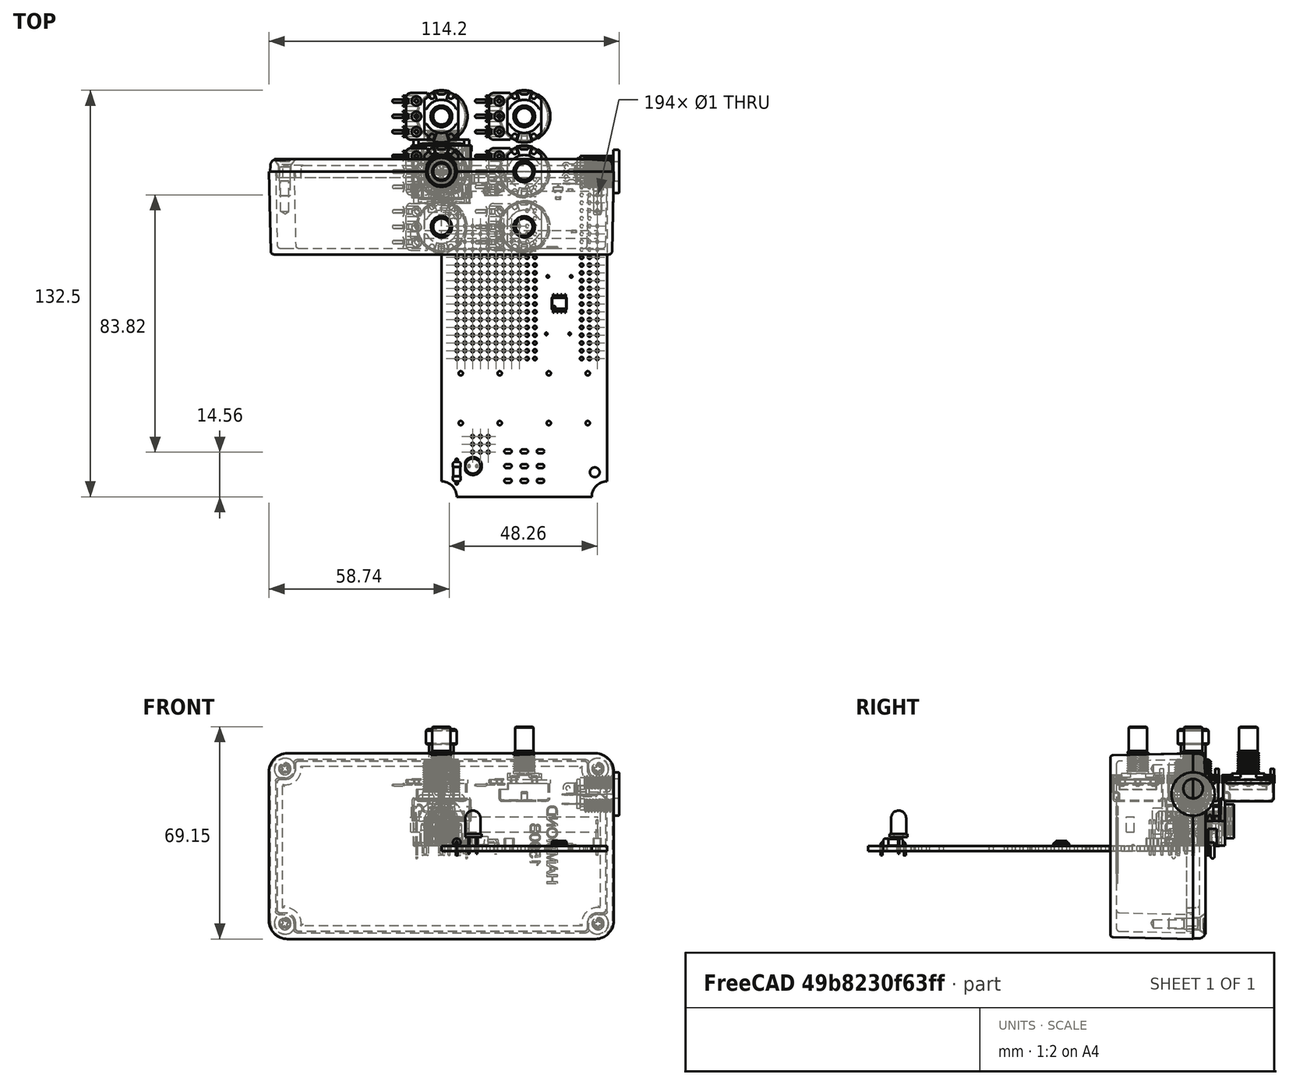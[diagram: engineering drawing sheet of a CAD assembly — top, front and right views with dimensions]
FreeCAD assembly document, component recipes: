
FREECAD ASSEMBLY — COMPONENT RECIPES ("1590Balt")

This assembly document has 3 components, labeled P0..P2 below (a component is one placed body or linked part). 0 of them carry a construction recipe — the FreeCAD feature program that regenerates the part from scratch, quoted from this document or its linked companion documents; the rest are supplied as boundary geometry only. No exploded tour is included for this assembly.
COMPONENT P0 — geometry summary ("kicad_pcb"; no construction recipe available for this part):
  bounding box: 106.0 x 55.4 x 42.3 mm
  tessellated surface: 165,730 triangles
  volume: 19802 mm^3 (8% of its bounding box)
COMPONENT P1 — geometry summary ("DC jack external v011"; no construction recipe available for this part):
  bounding box: 18.3 x 15.0 x 15.0 mm
  tessellated surface: 26,924 triangles
  volume: 1114 mm^3 (27% of its bounding box)
COMPONENT P2 — geometry summary ("1590B"; no construction recipe available for this part):
  bounding box: 112.4 x 60.5 x 31.0 mm
  tessellated surface: 55,694 triangles
  volume: 50075 mm^3 (24% of its bounding box)
  symmetry: 2-fold rotationally symmetric about the z axis; mirror-symmetric across its x mid-plane, y mid-plane
PROVENANCE & LICENSES
A FreeCAD (.FCStd) document from a public repository crawl; recipes are the document's own serialized feature recipes (and, for linked parts, companion documents' recipes).
License: gpl-3.0.
